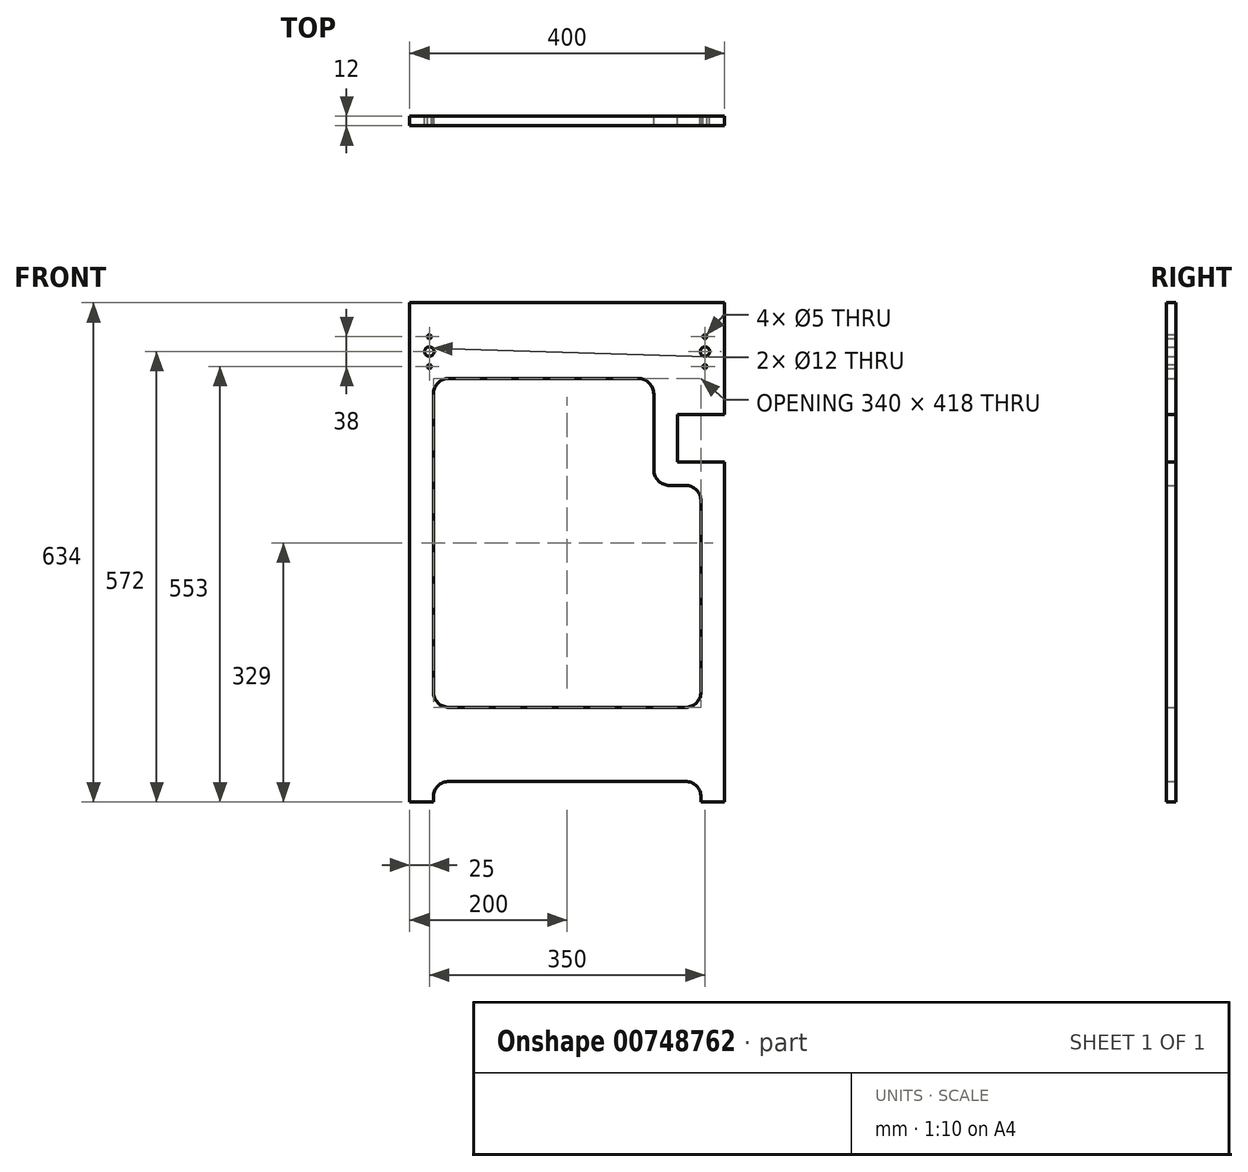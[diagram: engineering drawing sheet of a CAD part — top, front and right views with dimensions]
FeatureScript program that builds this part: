
annotation { "Feature Type Name" : "Feature", "Feature Type Description" : "" }
export const myFeature = defineFeature(function(context is Context, id is Id, definition is map)
    precondition{}
    {
        {
            assignVariable(context, id + "F0", {"name" : "Width", "anyValue" : 12});
        }
        {
            var Q0;
            Q0=qCreatedBy(makeId("Front.planeOp"),FACE);
            var sketch = newSketch(context, id + "F1", { "sketchPlane" : qUnion([Q0])});
            skLineSegment(sketch, "E0.bottom", {"start": v(90, 278) * mm, "end": v(-150, 278) * mm});
            skLineSegment(sketch, "E0.top", {"start": v(150, -140) * mm, "end": v(-150, -140) * mm});
            skLineSegment(sketch, "E0.left", {"start": v(170, 122) * mm, "end": v(170, -120) * mm});
            skLineSegment(sketch, "E0.right", {"start": v(-170, 258) * mm, "end": v(-170, -120) * mm});
            skLineSegment(sketch, "E1.bottom", {"start": v(200, 374) * mm, "end": v(-200, 374) * mm});
            skLineSegment(sketch, "E1.top", {"start": v(200, -260) * mm, "end": v(-200, -260) * mm});
            skLineSegment(sketch, "E1.left", {"start": v(200, 374) * mm, "end": v(200, -260) * mm});
            skLineSegment(sketch, "E1.right", {"start": v(-200, 374) * mm, "end": v(-200, -260) * mm});
            skLineSegment(sketch, "E2", {"start": v(-200, -222) * mm, "end": v(200, -222) * mm});
            skLineSegment(sketch, "E3", {"start": v(-200, -162) * mm, "end": v(200, -162) * mm});
            skLineSegment(sketch, "E4", {"start": v(-200, -150) * mm, "end": v(200, -150) * mm});
            skLineSegment(sketch, "E5", {"start": v(-170, -254) * mm, "end": v(-170, -260) * mm});
            skLineSegment(sketch, "E6", {"start": v(170, -254) * mm, "end": v(170, -260) * mm});
            skLineSegment(sketch, "E7", {"start": v(-150, -234) * mm, "end": v(150, -234) * mm});
            skArc(sketch, "E8.filletArc", {"start": v(-150, -234) * mm, "mid": v(-164.14, -239.86) * mm, "end": v(-170, -254) * mm});
            skArc(sketch, "E9.filletArc", {"start": v(170, -254) * mm, "mid": v(164.14, -239.86) * mm, "end": v(150, -234) * mm});
            skLineSegment(sketch, "E10", {"start": v(-150, -234) * mm, "end": v(-200, -234) * mm});
            skLineSegment(sketch, "E11", {"start": v(150, -234) * mm, "end": v(200, -234) * mm});
            skCircle(sketch, "E12", {"center": v(-175, 312) * mm, "radius": 6 * mm});
            skCircle(sketch, "E13", {"center": v(175, 312) * mm, "radius": 6 * mm});
            skCircle(sketch, "E14", {"center": v(175, 331) * mm, "radius": 2.5 * mm});
            skCircle(sketch, "E15", {"center": v(175, 293) * mm, "radius": 2.5 * mm});
            skCircle(sketch, "E16", {"center": v(-175, 331) * mm, "radius": 2.5 * mm});
            skCircle(sketch, "E17", {"center": v(-175, 293) * mm, "radius": 2.5 * mm});
            skPoint(sketch, "E18.visualSharp", {"position": v(-170, 278) * mm});
            skArc(sketch, "E18.filletArc", {"start": v(-150, 278) * mm, "mid": v(-164.14, 272.14) * mm, "end": v(-170, 258) * mm});
            skPoint(sketch, "E19.visualSharp", {"position": v(170, -140) * mm});
            skArc(sketch, "E19.filletArc", {"start": v(150, -140) * mm, "mid": v(164.14, -134.14) * mm, "end": v(170, -120) * mm});
            skPoint(sketch, "E20.visualSharp", {"position": v(-170, -140) * mm});
            skArc(sketch, "E20.filletArc", {"start": v(-170, -120) * mm, "mid": v(-164.14, -134.14) * mm, "end": v(-150, -140) * mm});
            skLineSegment(sketch, "E21.bottom", {"start": v(140, 172) * mm, "end": v(200, 172) * mm});
            skLineSegment(sketch, "E21.top", {"start": v(140, 232) * mm, "end": v(200, 232) * mm});
            skLineSegment(sketch, "E21.left", {"start": v(140, 172) * mm, "end": v(140, 232) * mm});
            skLineSegment(sketch, "E21.right", {"start": v(200, 172) * mm, "end": v(200, 232) * mm});
            skPoint(sketch, "E21.middle", {"position": v(170, 202) * mm});
            skLineSegment(sketch, "E22", {"start": v(110, 264.68) * mm, "end": v(110, 162) * mm});
            skLineSegment(sketch, "E23", {"start": v(130, 142) * mm, "end": v(150, 142) * mm});
            skLineSegment(sketch, "E24", {"start": v(110, 258) * mm, "end": v(110, 264.68) * mm});
            skPoint(sketch, "E25.visualSharp", {"position": v(110, 142) * mm});
            skArc(sketch, "E25.filletArc", {"start": v(110, 162) * mm, "mid": v(115.86, 147.86) * mm, "end": v(130, 142) * mm});
            skArc(sketch, "E26.filletArc", {"start": v(170, 122) * mm, "mid": v(164.14, 136.14) * mm, "end": v(150, 142) * mm});
            skArc(sketch, "E27.filletArc", {"start": v(110, 258) * mm, "mid": v(104.14, 272.14) * mm, "end": v(90, 278) * mm});
            skSolve(sketch);
        }
        {
            var Q0;
            Q0=makeQuery(id+"F1.imprint","IMPRINT",FACE,{"disambiguationData":[TD([[makeQuery(id+"F1.imprint","IMPRINT",EDGE,{"derivedFrom":sQuery(id+"F1.wireOp",EDGE,"E0.bottom")}),-1.0]])]});
            var Q1;
            {var subQ0=sQuery(id+"F1.wireOp",EDGE,"E3");Q1=makeQuery(id+"F1.imprint","IMPRINT",FACE,{"disambiguationData":[TD([[makeQuery(id+"F1.imprint","IMPRINT",EDGE,{"derivedFrom":subQ0}),1.0]])]});}
            var Q2;
            {var subQ0=sQuery(id+"F1.wireOp",EDGE,"E2");Q2=makeQuery(id+"F1.imprint","IMPRINT",FACE,{"disambiguationData":[TD([[makeQuery(id+"F1.imprint","IMPRINT",EDGE,{"derivedFrom":subQ0}),1.0]])]});}
            var Q3;
            {var subQ2=sQuery(id+"F1.wireOp",EDGE,"E2");Q3=makeQuery(id+"F1.imprint","IMPRINT",FACE,{"disambiguationData":[TD([[makeQuery(id+"F1.imprint","IMPRINT",EDGE,{"derivedFrom":subQ2}),-1.0]])]});}
            var Q4;
            {var subQ0=sQuery(id+"F1.wireOp",EDGE,"E6");Q4=makeQuery(id+"F1.imprint","IMPRINT",FACE,{"disambiguationData":[TD([[makeQuery(id+"F1.imprint","IMPRINT",EDGE,{"derivedFrom":subQ0}),1.0]])]});}
            var Q5;
            {var subQ0=sQuery(id+"F1.wireOp",EDGE,"E5");Q5=makeQuery(id+"F1.imprint","IMPRINT",FACE,{"disambiguationData":[TD([[makeQuery(id+"F1.imprint","IMPRINT",EDGE,{"derivedFrom":subQ0}),-1.0]])]});}
            extrude(context, id + "F2", {"entities" : qUnion([Q0, Q1, Q2, Q3, Q4, Q5]), "depth" : (getVariable(context, 'Width')) * mm, "offsetDistance" : 25 * mm});
        }
    });
